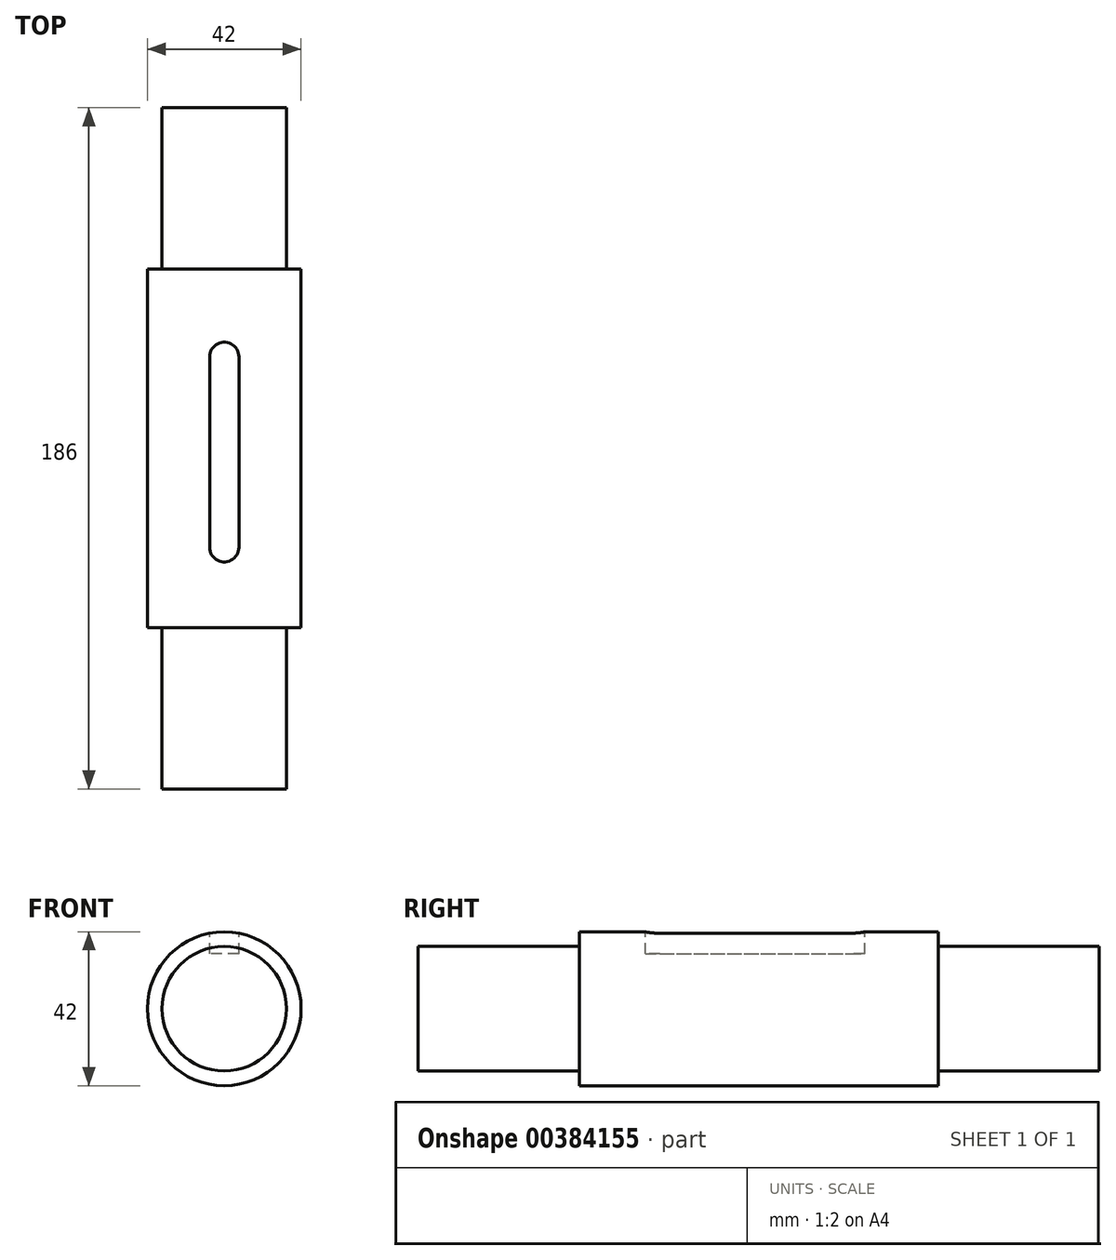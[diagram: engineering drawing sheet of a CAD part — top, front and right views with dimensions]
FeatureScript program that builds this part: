
annotation { "Feature Type Name" : "Feature", "Feature Type Description" : "" }
export const myFeature = defineFeature(function(context is Context, id is Id, definition is map)
    precondition{}
    {
        {
            var Q0;
            Q0=qCreatedBy(makeId("Front.planeOp"),FACE);
            var sketch = newSketch(context, id + "F0", { "sketchPlane" : qUnion([Q0])});
            skCircle(sketch, "E0", {"center": v(0, 0) * mm, "radius": 21 * mm});
            skSolve(sketch);
        }
        {
            var Q0;
            Q0 = qSketchRegion(id + "F0", true);
            extrude(context, id + "F1", {"entities" : qUnion([Q0]), "depth" : 186 * mm});
        }
        {
            var Q0;
            Q0=makeQuery(id+"F1.opExtrude","CAP_FACE",FACE,{"disambiguationData":[OSD([sQuery(id+"F0.wireOp",EDGE,"E0")])],"isStart":false});
            var sketch = newSketch(context, id + "F2", { "sketchPlane" : qUnion([Q0])});
            skCircle(sketch, "E1", {"center": v(0, 0) * mm, "radius": 17 * mm});
            skSolve(sketch);
        }
        {
            var Q0;
            Q0=makeQuery(id+"F1.opExtrude","CAP_FACE",FACE,{"disambiguationData":[OSD([sQuery(id+"F0.wireOp",EDGE,"E0")])],"isStart":true});
            var sketch = newSketch(context, id + "F3", { "sketchPlane" : qUnion([Q0])});
            skCircle(sketch, "E2", {"center": v(0, 0) * mm, "radius": 17 * mm});
            skSolve(sketch);
        }
        {
            var Q0;
            Q0=makeQuery(id+"F3.imprint","IMPRINT",FACE,{"disambiguationData":[TD([[makeQuery(id+"F3.imprint","IMPRINT",EDGE,{"derivedFrom":sQuery(id+"F3.wireOp",EDGE,"E2")}),-1.0]])]});
            extrude(context, id + "F4", {"entities" : qUnion([Q0]), "operationType" : NewBodyOperationType.REMOVE, "oppositeDirection" : true, "depth" : 44 * mm});
        }
        {
            var Q0;
            Q0=makeQuery(id+"F2.imprint","IMPRINT",FACE,{"disambiguationData":[TD([[makeQuery(id+"F2.imprint","IMPRINT",EDGE,{"derivedFrom":sQuery(id+"F2.wireOp",EDGE,"E1")}),-1.0]])]});
            extrude(context, id + "F5", {"entities" : qUnion([Q0]), "operationType" : NewBodyOperationType.REMOVE, "oppositeDirection" : true, "depth" : 44 * mm});
        }
        {
            var Q0;
            Q0=qCreatedBy(makeId("Top.planeOp"),FACE);
            cPlane(context, id + "F6", {"entities" : qUnion([Q0]), "cplaneType" : CPlaneType.OFFSET, "offset" : 21 * mm, "width" : 150 * mm, "height" : 150 * mm});
        }
        {
            var Q0;
            Q0=qCreatedBy(id+"F6.planeOp",FACE);
            var sketch = newSketch(context, id + "F7", { "sketchPlane" : qUnion([Q0])});
            skLineSegment(sketch, "E3.bottom", {"start": v(0, -68) * mm, "end": v(4, -68) * mm});
            skLineSegment(sketch, "E3.top", {"start": v(0, -120) * mm, "end": v(4, -120) * mm});
            skLineSegment(sketch, "E3.left", {"start": v(0, -68) * mm, "end": v(0, -120) * mm});
            skLineSegment(sketch, "E3.right", {"start": v(4, -68) * mm, "end": v(4, -120) * mm});
            skSolve(sketch);
        }
        {
            var Q0;
            Q0=makeQuery(id+"F7.imprint","IMPRINT",FACE,{"disambiguationData":[TD([[makeQuery(id+"F7.imprint","IMPRINT",EDGE,{"derivedFrom":sQuery(id+"F7.wireOp",EDGE,"E3.bottom")}),-1.0]])]});
            extrude(context, id + "F8", {"entities" : qUnion([Q0]), "operationType" : NewBodyOperationType.REMOVE, "oppositeDirection" : true, "depth" : 6 * mm});
        }
        {
            var Q0;
            Q0=makeQuery(id+"F8.boolean.opBoolean","COPY",FACE,{"derivedFrom":makeQuery(id+"F8.opExtrude","SWEPT_FACE",FACE,{"disambiguationData":[OSD([sQuery(id+"F7.wireOp",EDGE,"E3.left")])]})});
            extrude(context, id + "F9", {"entities" : qUnion([Q0]), "operationType" : NewBodyOperationType.REMOVE, "oppositeDirection" : true, "depth" : 4 * mm});
        }
        {
            var Q0;
            Q0=qCreatedBy(id+"F6.planeOp",FACE);
            var sketch = newSketch(context, id + "F10", { "sketchPlane" : qUnion([Q0])});
            skArc(sketch, "E4", {"start": v(4, -68.02) * mm, "mid": v(0.02, -64) * mm, "end": v(-4, -67.98) * mm});
            skArc(sketch, "E5", {"start": v(-4, -119.98) * mm, "mid": v(-0.02, -124) * mm, "end": v(4, -120.02) * mm});
            skLineSegment(sketch, "E6", {"start": v(-4, -67.98) * mm, "end": v(4, -68.02) * mm});
            skLineSegment(sketch, "E7", {"start": v(-4, -119.98) * mm, "end": v(4, -120.02) * mm});
            skSolve(sketch);
        }
        {
            var Q0;
            Q0=makeQuery(id+"F10.imprint","IMPRINT",FACE,{"disambiguationData":[TD([[makeQuery(id+"F10.imprint","IMPRINT",EDGE,{"derivedFrom":sQuery(id+"F10.wireOp",EDGE,"E5")}),1.0]])]});
            extrude(context, id + "F11", {"entities" : qUnion([Q0]), "operationType" : NewBodyOperationType.REMOVE, "oppositeDirection" : true, "depth" : 6 * mm});
        }
        {
            var Q0;
            Q0=makeQuery(id+"F11.boolean.opBoolean","COPY",FACE,{"derivedFrom":makeQuery(id+"F11.opExtrude","SWEPT_FACE",FACE,{"disambiguationData":[OSD([sQuery(id+"F10.wireOp",EDGE,"E7")])]})});
            extrude(context, id + "F12", {"entities" : qUnion([Q0]), "operationType" : NewBodyOperationType.REMOVE, "oppositeDirection" : true, "depth" : 1 * mm});
        }
        {
            var Q0;
            Q0 = qSketchRegion(id + "F10", true);
            extrude(context, id + "F13", {"entities" : qUnion([Q0]), "operationType" : NewBodyOperationType.REMOVE, "oppositeDirection" : true, "depth" : 6 * mm});
        }
        {
            var Q0;
            Q0=makeQuery(id+"F13.boolean.opBoolean","COPY",FACE,{"derivedFrom":makeQuery(id+"F13.opExtrude","SWEPT_FACE",FACE,{"disambiguationData":[OSD([sQuery(id+"F10.wireOp",EDGE,"E6")])]})});
            extrude(context, id + "F14", {"entities" : qUnion([Q0]), "operationType" : NewBodyOperationType.REMOVE, "oppositeDirection" : true, "depth" : 1 * mm});
        }
    });
